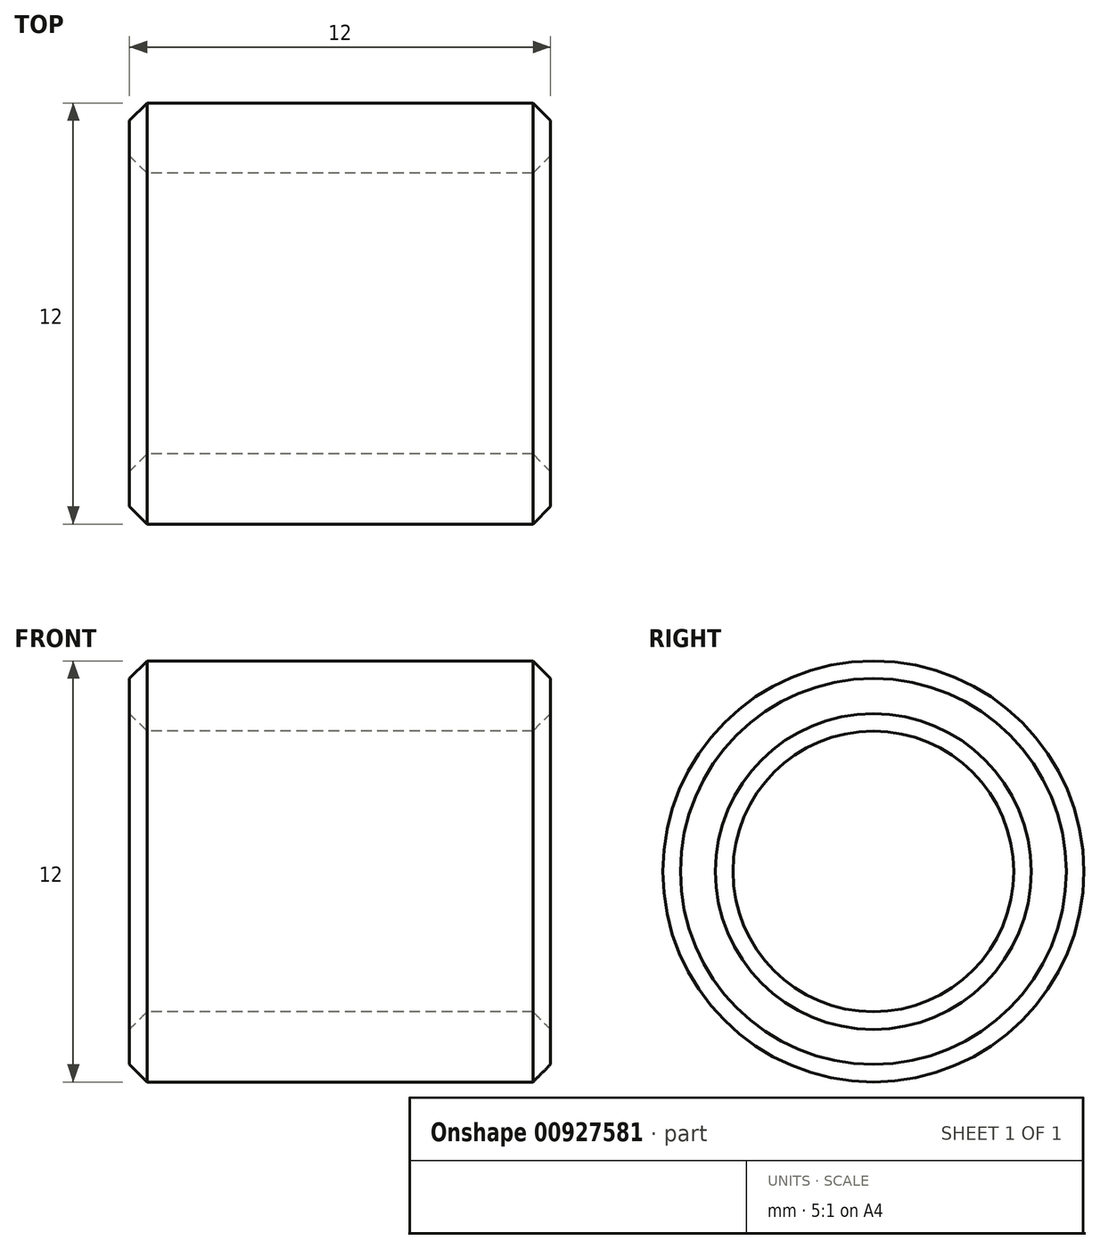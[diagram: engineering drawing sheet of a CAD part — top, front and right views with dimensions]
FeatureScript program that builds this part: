
annotation { "Feature Type Name" : "Feature", "Feature Type Description" : "" }
export const myFeature = defineFeature(function(context is Context, id is Id, definition is map)
    precondition{}
    {
        {
            var Q0;
            Q0=qCreatedBy(makeId("Right.planeOp"),FACE);
            var sketch = newSketch(context, id + "F0", { "sketchPlane" : qUnion([Q0])});
            skCircle(sketch, "E0", {"center": v(0, 0) * mm, "radius": 4 * mm});
            skCircle(sketch, "E1.0", {"center": v(0, 0) * mm, "radius": 6 * mm});
            skSolve(sketch);
        }
        {
            var Q0;
            Q0 = qSketchRegion(id + "F0", true);
            extrude(context, id + "F1", {"entities" : qUnion([Q0]), "depth" : 12 * mm, "offsetDistance" : 25 * mm});
        }
        {
            var Q0;
            Q0=makeQuery(id+"F1.opExtrude","CAP_EDGE",EDGE,{"disambiguationData":[OSD([sQuery(id+"F0.wireOp",EDGE,"E1.0")])],"isStart":false});
            var Q1;
            Q1=makeQuery(id+"F1.opExtrude","CAP_EDGE",EDGE,{"disambiguationData":[OSD([sQuery(id+"F0.wireOp",EDGE,"E0")])],"isStart":false});
            var Q2;
            Q2=makeQuery(id+"F1.opExtrude","CAP_EDGE",EDGE,{"disambiguationData":[OSD([sQuery(id+"F0.wireOp",EDGE,"E1.0")])],"isStart":true});
            var Q3;
            Q3=makeQuery(id+"F1.opExtrude","CAP_EDGE",EDGE,{"disambiguationData":[OSD([sQuery(id+"F0.wireOp",EDGE,"E0")])],"isStart":true});
            chamfer(context, id + "F2", {"entities" : qUnion([Q0, Q1, Q2, Q3]), "width" : 0.5 * mm, "tangentPropagation" : true});
        }
    });
